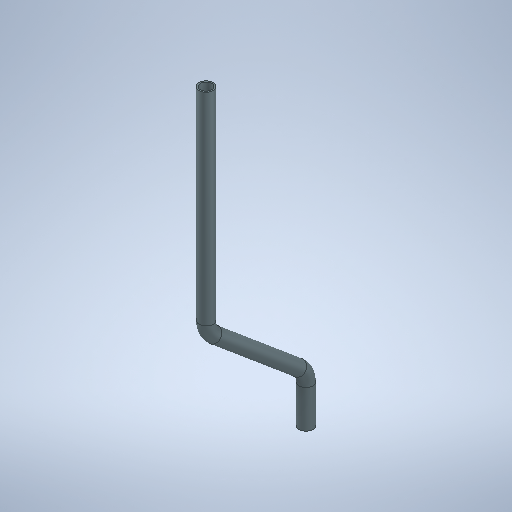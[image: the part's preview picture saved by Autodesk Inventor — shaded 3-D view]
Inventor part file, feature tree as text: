
AUTODESK INVENTOR PART (.ipt)
format: ipt  version: 2025.1 (Build 291241000, 241)  size: 281,600 bytes
history: native  units: mm
features: sketch x2, sweep x1, shell x1
ambient origin geometry x8: Origin, YZ Plane, XZ Plane, XY Plane, X Axis, Y Axis, Z Axis, Center Point
bodies: Solid1 (feature_tree)
feature tree (4):
  sweep  "Sweep1"
  shell  "Shell1"  Thickness=35.75mm
  sketch  "Sketch1"  dims[d0=5.0mm d1=76.0mm d2=35.75mm]
  sketch  "Sketch2"  dims[d3=17.0mm d4=30.0mm d5=7.5mm d6=0.0mm d7=0.0mm d8=0.5mm]
